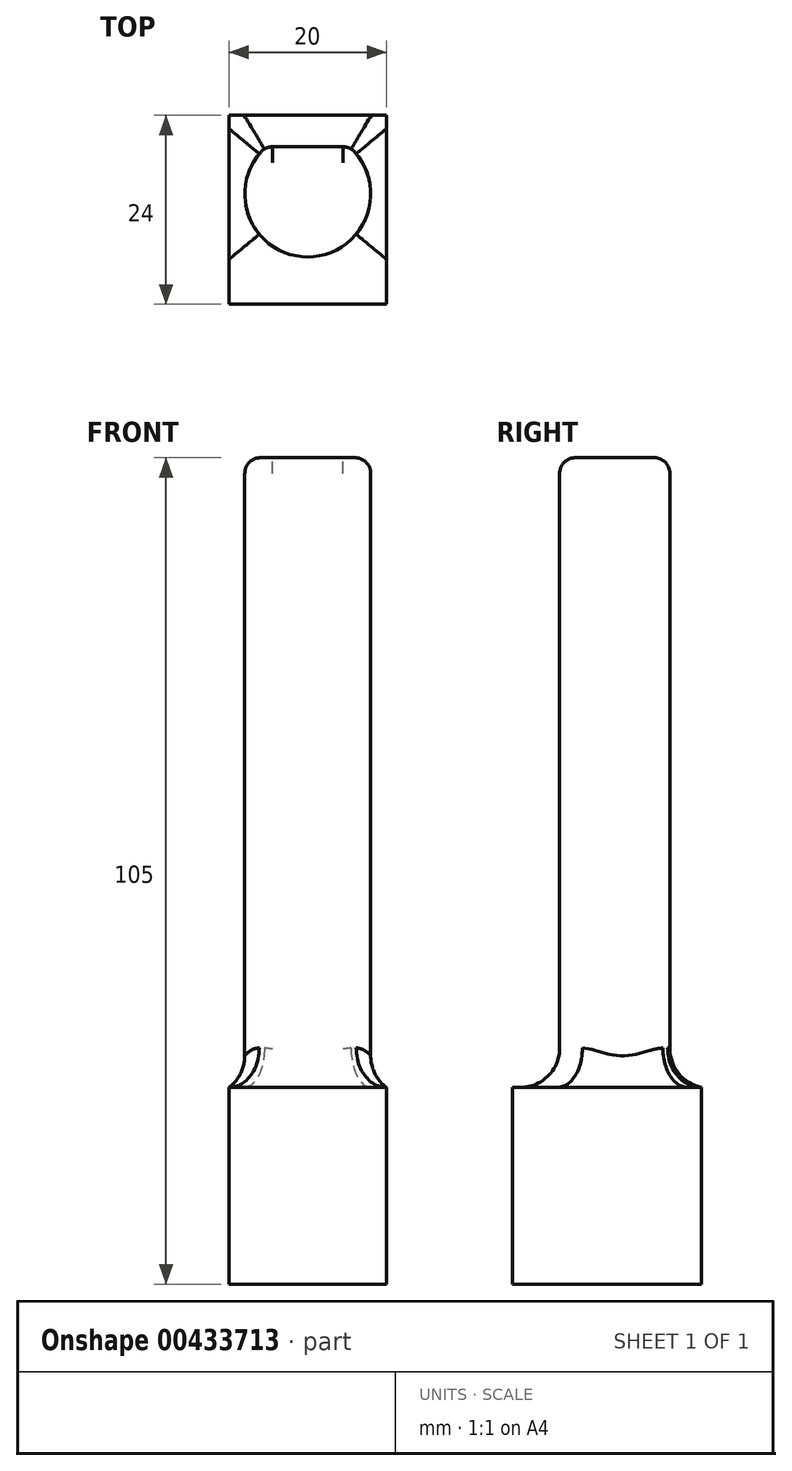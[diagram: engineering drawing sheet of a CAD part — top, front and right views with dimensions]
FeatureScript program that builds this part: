
annotation { "Feature Type Name" : "Feature", "Feature Type Description" : "" }
export const myFeature = defineFeature(function(context is Context, id is Id, definition is map)
    precondition{}
    {
        {
            var Q0;
            Q0=qCreatedBy(makeId("Top.planeOp"),FACE);
            var sketch = newSketch(context, id + "F0", { "sketchPlane" : qUnion([Q0])});
            skArc(sketch, "E0", {"start": v(-5.3, 6) * mm, "mid": v(0, -8) * mm, "end": v(5.3, 6) * mm});
            skLineSegment(sketch, "E1", {"start": v(-5.3, 6) * mm, "end": v(5.3, 6) * mm});
            skSolve(sketch);
        }
        {
            var Q0;
            Q0=makeQuery(id+"F0.imprint","IMPRINT",FACE,{"disambiguationData":[TD([[makeQuery(id+"F0.imprint","IMPRINT",EDGE,{"derivedFrom":sQuery(id+"F0.wireOp",EDGE,"E0")}),1.0]])]});
            extrude(context, id + "F1", {"entities" : qUnion([Q0]), "depth" : 80 * mm});
        }
        {
            var Q0;
            Q0=makeQuery(id+"F1.opExtrude","CAP_EDGE",EDGE,{"disambiguationData":[OSD([sQuery(id+"F0.wireOp",EDGE,"E1")])],"isStart":false});
            fillet(context, id + "F2", {"entities" : qUnion([Q0]), "radius" : 2 * mm, "tangentPropagation" : true, "allowEdgeOverflow" : false});
        }
        {
            var Q0;
            Q0=makeQuery(id+"F1.opExtrude","CAP_EDGE",EDGE,{"disambiguationData":[OSD([sQuery(id+"F0.wireOp",EDGE,"E0")])],"isStart":false});
            fillet(context, id + "F3", {"entities" : qUnion([Q0]), "radius" : 2 * mm, "tangentPropagation" : true, "allowEdgeOverflow" : false});
        }
        {
            var Q0;
            Q0=qCreatedBy(makeId("Top.planeOp"),FACE);
            var sketch = newSketch(context, id + "F4", { "sketchPlane" : qUnion([Q0])});
            skLineSegment(sketch, "E2.bottom", {"start": v(-10, -14) * mm, "end": v(10, -14) * mm});
            skLineSegment(sketch, "E2.top", {"start": v(-10, 10) * mm, "end": v(10, 10) * mm});
            skLineSegment(sketch, "E2.left", {"start": v(-10, -14) * mm, "end": v(-10, 10) * mm});
            skLineSegment(sketch, "E2.right", {"start": v(10, -14) * mm, "end": v(10, 10) * mm});
            skSolve(sketch);
        }
        {
            var Q0;
            Q0=makeQuery(id+"F4.imprint","IMPRINT",FACE,{"disambiguationData":[TD([[makeQuery(id+"F4.imprint","IMPRINT",EDGE,{"derivedFrom":sQuery(id+"F4.wireOp",EDGE,"E2.bottom")}),1.0]])]});
            extrude(context, id + "F5", {"entities" : qUnion([Q0]), "operationType" : NewBodyOperationType.ADD, "oppositeDirection" : true, "depth" : 25 * mm});
        }
        {
            var Q0;
            Q0=makeQuery(id+"F1.opExtrude","SWEPT_FACE",FACE,{"disambiguationData":[OSD([sQuery(id+"F0.wireOp",EDGE,"E1")])]});
            fillet(context, id + "F6", {"entities" : qUnion([Q0]), "radius" : 5 * mm, "tangentPropagation" : true, "allowEdgeOverflow" : false});
        }
    });
